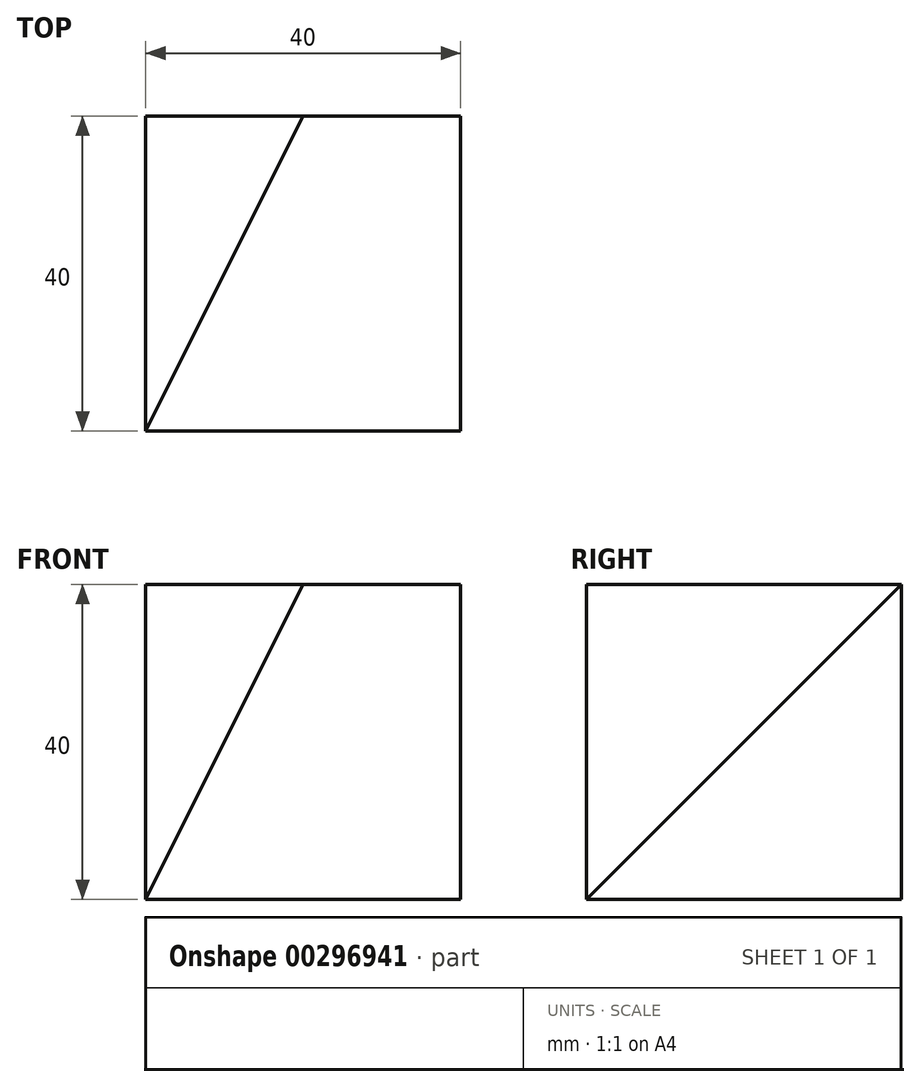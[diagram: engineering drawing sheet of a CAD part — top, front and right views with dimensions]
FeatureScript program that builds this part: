
annotation { "Feature Type Name" : "Feature", "Feature Type Description" : "" }
export const myFeature = defineFeature(function(context is Context, id is Id, definition is map)
    precondition{}
    {
        {
            var Q0;
            Q0=qCreatedBy(makeId("Right.planeOp"),FACE);
            var sketch = newSketch(context, id + "F0", { "sketchPlane" : qUnion([Q0])});
            skLineSegment(sketch, "E0.bottom", {"start": v(0, 0) * mm, "end": v(40, 0) * mm});
            skLineSegment(sketch, "E0.top", {"start": v(0, 40) * mm, "end": v(40, 40) * mm});
            skLineSegment(sketch, "E0.left", {"start": v(0, 0) * mm, "end": v(0, 40) * mm});
            skLineSegment(sketch, "E0.right", {"start": v(40, 0) * mm, "end": v(40, 40) * mm});
            skLineSegment(sketch, "E1", {"start": v(0, 0) * mm, "end": v(40, 40) * mm});
            skSolve(sketch);
        }
        {
            var Q0;
            Q0=makeQuery(id+"F0.imprint","IMPRINT",FACE,{"disambiguationData":[TD([[makeQuery(id+"F0.imprint","IMPRINT",EDGE,{"derivedFrom":sQuery(id+"F0.wireOp",EDGE,"E0.bottom")}),1.0]])]});
            extrude(context, id + "F1", {"entities" : qUnion([Q0]), "depth" : 40 * mm});
        }
        {
            var Q0;
            Q0=makeQuery(id+"F1.opExtrude","SWEPT_FACE",FACE,{"disambiguationData":[OSD([sQuery(id+"F0.wireOp",EDGE,"E0.bottom")])]});
            var sketch = newSketch(context, id + "F2", { "sketchPlane" : qUnion([Q0])});
            skLineSegment(sketch, "E2", {"start": v(0, 0) * mm, "end": v(20, -40) * mm});
            skSolve(sketch);
        }
        {
            var Q0;
            Q0 = qSketchRegion(id + "F2", true);
            var Q1;
            {var subQ0=sQuery(id+"F2.wireOp",EDGE,"E2");Q1=makeQuery(id+"F2.imprint","IMPRINT",FACE,{"disambiguationData":[TD([[makeQuery(id+"F2.imprint","IMPRINT",EDGE,{"derivedFrom":subQ0}),-1.0]])]});}
            extrude(context, id + "F3", {"entities" : qUnion([Q0, Q1]), "operationType" : NewBodyOperationType.ADD, "oppositeDirection" : true, "depth" : 40 * mm});
        }
        {
            var Q0;
            Q0=makeQuery(id+"F3.opExtrude","CAP_VERTEX",VERTEX,{"disambiguationData":[OSD([sQuery(id+"F0.wireOp",EDGE,"E0.bottom"),sQuery(id+"F0.wireOp",EDGE,"E0.left"),sQuery(id+"F0.wireOp",EDGE,"E1"),sQuery(id+"F2.wireOp",EDGE,"E2")])],"isStart":false});
            var Q1;
            Q1=makeQuery(id+"F3.opExtrude","CAP_VERTEX",VERTEX,{"disambiguationData":[OSD([sQuery(id+"F0.wireOp",EDGE,"E0.bottom"),sQuery(id+"F0.wireOp",EDGE,"E0.right"),sQuery(id+"F2.wireOp",EDGE,"E2")])],"isStart":false});
            var Q2;
            Q2=makeQuery(id+"F1.opExtrude","CAP_VERTEX",VERTEX,{"disambiguationData":[OSD([sQuery(id+"F0.wireOp",EDGE,"E0.bottom"),sQuery(id+"F0.wireOp",EDGE,"E0.right")])],"isStart":true});
            cPlane(context, id + "F4", {"entities" : qUnion([Q0, Q1, Q2]), "cplaneType" : CPlaneType.THREE_POINT, "offset" : 25 * mm, "width" : 150 * mm, "height" : 150 * mm});
        }
        {
            var Q0;
            Q0=qCreatedBy(id+"F4.planeOp",FACE);
            var sketch = newSketch(context, id + "F5", { "sketchPlane" : qUnion([Q0])});
            skPoint(sketch, "E3.0", {"position": v(36.51, 44.72) * mm});
            skPoint(sketch, "E4.0", {"position": v(-7.3, 35.78) * mm});
            skPoint(sketch, "E5.0", {"position": v(36.51, 0) * mm});
            skLineSegment(sketch, "E6", {"start": v(36.51, 44.72) * mm, "end": v(36.51, 0) * mm});
            skLineSegment(sketch, "E7", {"start": v(-7.3, 35.78) * mm, "end": v(36.51, 0) * mm});
            skLineSegment(sketch, "E8", {"start": v(-7.3, 35.78) * mm, "end": v(36.51, 44.72) * mm});
            skSolve(sketch);
        }
        {
            var Q0;
            Q0 = qSketchRegion(id + "F5", true);
            extrude(context, id + "F6", {"entities" : qUnion([Q0]), "operationType" : NewBodyOperationType.REMOVE, "endBound" : BoundingType.THROUGH_ALL, "oppositeDirection" : true, "depth" : 25 * mm});
        }
    });
